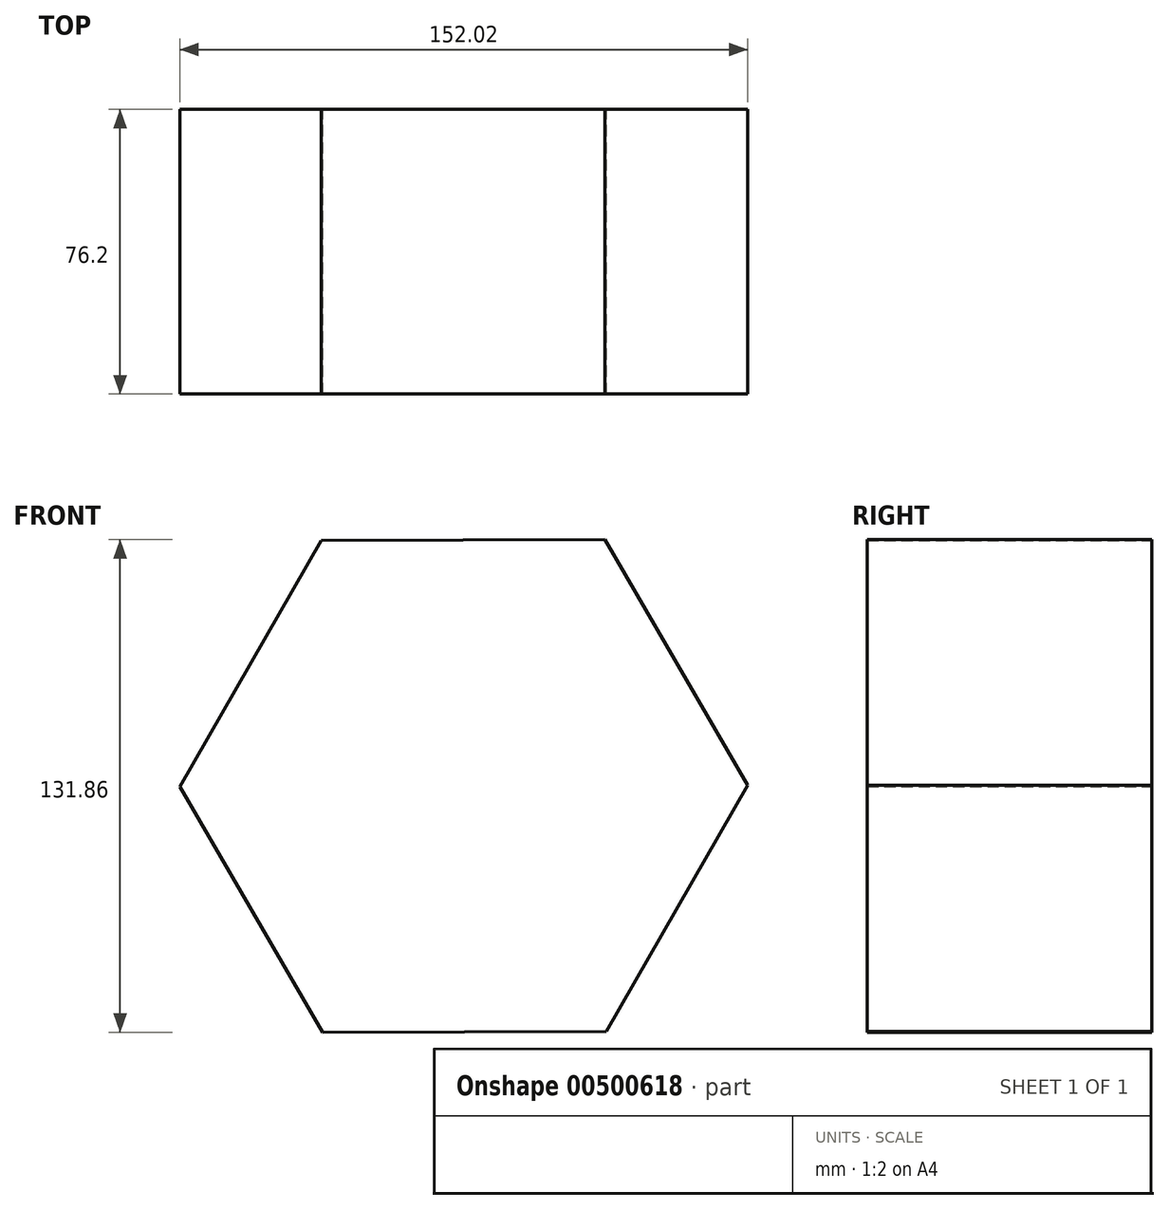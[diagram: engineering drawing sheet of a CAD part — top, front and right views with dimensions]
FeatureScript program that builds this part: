
annotation { "Feature Type Name" : "Feature", "Feature Type Description" : "" }
export const myFeature = defineFeature(function(context is Context, id is Id, definition is map)
    precondition{}
    {
        {
            var Q0;
            Q0=qCreatedBy(makeId("Front.planeOp"),FACE);
            var sketch = newSketch(context, id + "F0", { "sketchPlane" : qUnion([Q0])});
            skCircle(sketch, "E0.cCircle", {"center": v(0, 0) * mm, "radius": 76.01 * mm, "construction": true});
            skLineSegment(sketch, "E0.0", {"start": v(37.83, 65.93) * mm, "end": v(76.01, 0.2) * mm});
            skLineSegment(sketch, "E0.1", {"start": v(76.01, 0.2) * mm, "end": v(38.18, -65.73) * mm});
            skLineSegment(sketch, "E0.2", {"start": v(38.18, -65.73) * mm, "end": v(-37.83, -65.93) * mm});
            skLineSegment(sketch, "E0.3", {"start": v(-37.83, -65.93) * mm, "end": v(-76.01, -0.2) * mm});
            skLineSegment(sketch, "E0.4", {"start": v(-76.01, -0.2) * mm, "end": v(-38.18, 65.73) * mm});
            skLineSegment(sketch, "E0.5", {"start": v(-38.18, 65.73) * mm, "end": v(37.83, 65.93) * mm});
            skSolve(sketch);
        }
        {
            var Q0;
            Q0=makeQuery(id+"F0.imprint","IMPRINT",FACE,{"disambiguationData":[TD([[makeQuery(id+"F0.imprint","IMPRINT",EDGE,{"derivedFrom":sQuery(id+"F0.wireOp",EDGE,"E0.0")}),-1.0]])]});
            extrude(context, id + "F1", {"entities" : qUnion([Q0]), "depth" : 76.2 * mm});
        }
    });
